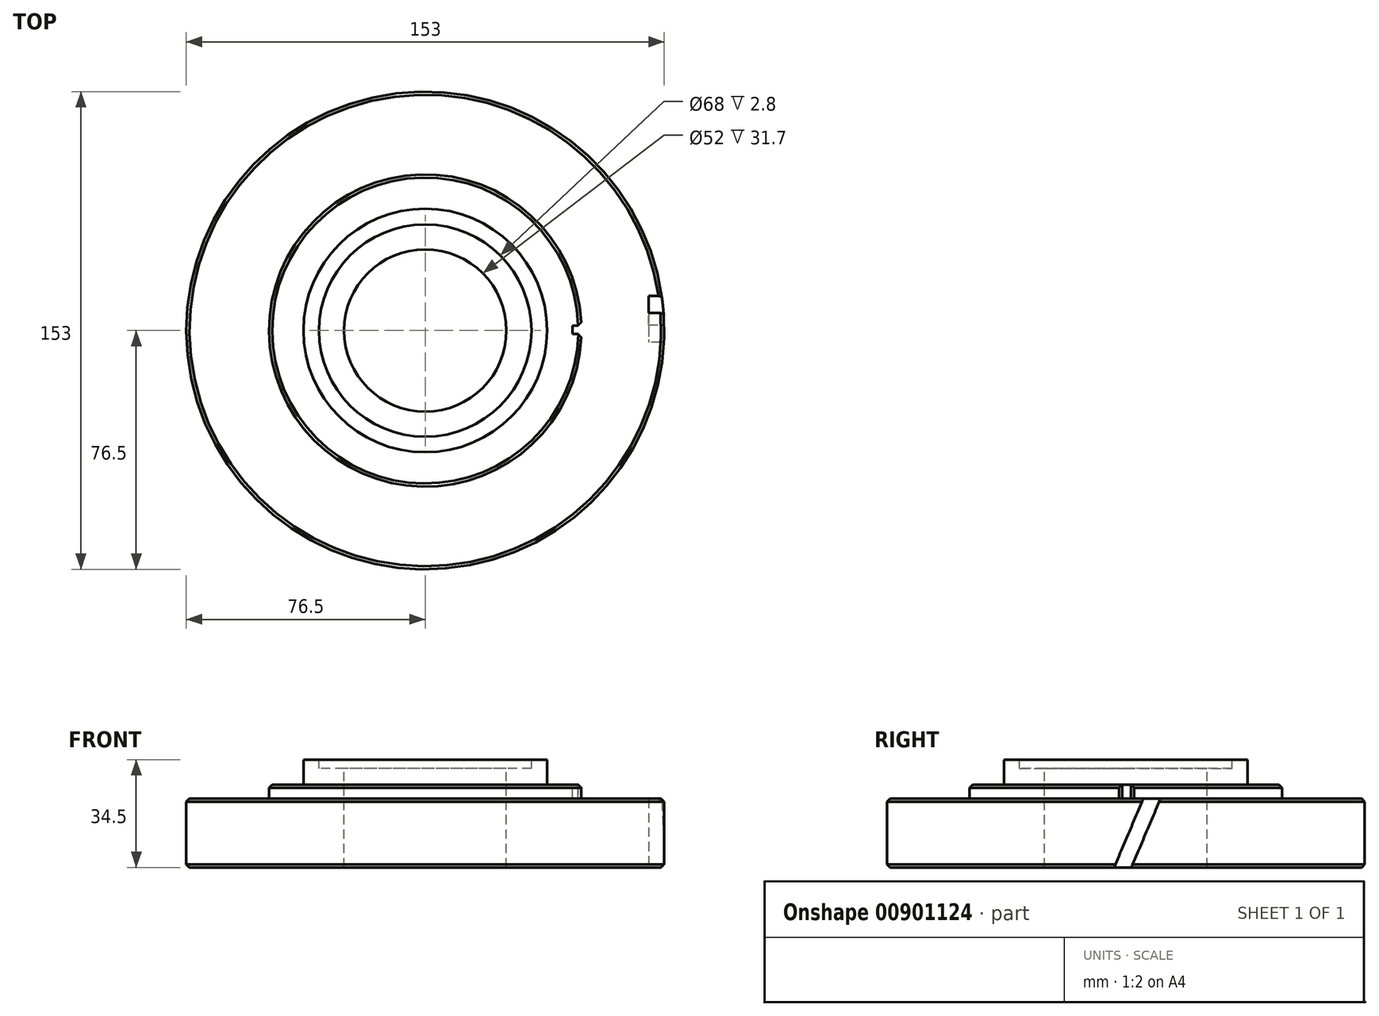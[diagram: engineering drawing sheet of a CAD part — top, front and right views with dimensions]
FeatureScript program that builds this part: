
annotation { "Feature Type Name" : "Feature", "Feature Type Description" : "" }
export const myFeature = defineFeature(function(context is Context, id is Id, definition is map)
    precondition{}
    {
        {
            var Q0;
            Q0=qCreatedBy(makeId("Front.planeOp"),FACE);
            var sketch = newSketch(context, id + "F0", { "sketchPlane" : qUnion([Q0])});
            skLineSegment(sketch, "E0", {"start": v(0, 34.5) * mm, "end": v(-39, 34.5) * mm});
            skLineSegment(sketch, "E1", {"start": v(-39, 34.5) * mm, "end": v(-39, 26.5) * mm});
            skLineSegment(sketch, "E2", {"start": v(-39, 26.5) * mm, "end": v(-50, 26.5) * mm});
            skLineSegment(sketch, "E3", {"start": v(-50, 26.5) * mm, "end": v(-50, 22) * mm});
            skLineSegment(sketch, "E4", {"start": v(-50, 22) * mm, "end": v(-76.5, 22) * mm});
            skLineSegment(sketch, "E5", {"start": v(-76.5, 22) * mm, "end": v(-76.5, 0) * mm});
            skLineSegment(sketch, "E6", {"start": v(-76.5, 0) * mm, "end": v(0, 0) * mm});
            skLineSegment(sketch, "E7", {"start": v(0, 0) * mm, "end": v(0, 34.5) * mm});
            skLineSegment(sketch, "E8", {"start": v(0, 59.57) * mm, "end": v(0, -27.66) * mm, "construction": true});
            skSolve(sketch);
        }
        {
            var Q0;
            Q0=makeQuery(id+"F0.imprint","IMPRINT",FACE,{"disambiguationData":[TD([[makeQuery(id+"F0.imprint","IMPRINT",EDGE,{"derivedFrom":sQuery(id+"F0.wireOp",EDGE,"E0")}),1.0]])]});
            var Q1;
            Q1=sQuery(id+"F0.wireOp",EDGE,"E8");
            revolve(context, id + "F1", {"surfaceOperationType" : NewSurfaceOperationType.NEW, "entities" : qUnion([Q0]), "axis" : qUnion([Q1]), "revolveType" : RevolveType.FULL});
        }
        {
            var Q0;
            Q0=makeQuery(id+"F1.opRevolve","SWEPT_FACE",FACE,{"disambiguationData":[OSD([sQuery(id+"F0.wireOp",EDGE,"E0")])]});
            var sketch = newSketch(context, id + "F2", { "sketchPlane" : qUnion([Q0])});
            skCircle(sketch, "E9", {"center": v(0, 0) * mm, "radius": 34 * mm});
            skSolve(sketch);
        }
        {
            var Q0;
            Q0 = qSketchRegion(id + "F2", true);
            extrude(context, id + "F3", {"entities" : qUnion([Q0]), "operationType" : NewBodyOperationType.REMOVE, "oppositeDirection" : true, "depth" : 2.8 * mm, "offsetDistance" : 25 * mm});
        }
        {
            var Q0;
            Q0=makeQuery(id+"F3.boolean.opBoolean","COPY",FACE,{"derivedFrom":makeQuery(id+"F3.opExtrude","CAP_FACE",FACE,{"disambiguationData":[OSD([sQuery(id+"F2.wireOp",EDGE,"E9")])],"isStart":false})});
            var sketch = newSketch(context, id + "F4", { "sketchPlane" : qUnion([Q0])});
            skCircle(sketch, "E10", {"center": v(0, 0) * mm, "radius": 26 * mm});
            skSolve(sketch);
        }
        {
            var Q0;
            Q0 = qSketchRegion(id + "F4", true);
            extrude(context, id + "F5", {"entities" : qUnion([Q0]), "operationType" : NewBodyOperationType.REMOVE, "endBound" : BoundingType.THROUGH_ALL, "oppositeDirection" : true, "depth" : 25 * mm, "offsetDistance" : 25 * mm});
        }
        {
            var Q0;
            Q0=qCreatedBy(makeId("Right.planeOp"),FACE);
            cPlane(context, id + "F6", {"entities" : qUnion([Q0]), "cplaneType" : CPlaneType.OFFSET, "offset" : 96.5 * mm, "width" : 150 * mm, "height" : 150 * mm});
        }
        {
            var Q0;
            Q0=qCreatedBy(id+"F6.planeOp",FACE);
            var sketch = newSketch(context, id + "F7", { "sketchPlane" : qUnion([Q0])});
            skLineSegment(sketch, "E11", {"start": v(12.66, 38.66) * mm, "end": v(-8.9, -12.16) * mm});
            skLineSegment(sketch, "E12", {"start": v(-8.9, -12.16) * mm, "end": v(-3.4, -12.16) * mm});
            skLineSegment(sketch, "E13", {"start": v(-3.4, -12.16) * mm, "end": v(18, 38.25) * mm});
            skLineSegment(sketch, "E14", {"start": v(18, 38.25) * mm, "end": v(12.66, 38.66) * mm});
            skSolve(sketch);
        }
        {
            var Q0;
            Q0=makeQuery(id+"F1.opRevolve","SWEPT_EDGE",EDGE,{"disambiguationData":[OSD([sQuery(id+"F0.wireOp",EDGE,"E4"),sQuery(id+"F0.wireOp",EDGE,"E5")])]});
            var Q1;
            Q1=makeQuery(id+"F1.opRevolve","SWEPT_EDGE",EDGE,{"disambiguationData":[OSD([sQuery(id+"F0.wireOp",EDGE,"E5"),sQuery(id+"F0.wireOp",EDGE,"E6")])]});
            var Q2;
            Q2=makeQuery(id+"F1.opRevolve","SWEPT_EDGE",EDGE,{"disambiguationData":[OSD([sQuery(id+"F0.wireOp",EDGE,"E2"),sQuery(id+"F0.wireOp",EDGE,"E3")])]});
            chamfer(context, id + "F8", {"entities" : qUnion([Q0, Q1, Q2]), "width" : 1 * mm, "tangentPropagation" : true});
        }
        {
            var Q0;
            Q0=makeQuery(id+"F7.imprint","IMPRINT",FACE,{"disambiguationData":[TD([[makeQuery(id+"F7.imprint","IMPRINT",EDGE,{"derivedFrom":sQuery(id+"F7.wireOp",EDGE,"E11")}),1.0]])]});
            extrude(context, id + "F9", {"entities" : qUnion([Q0]), "operationType" : NewBodyOperationType.REMOVE, "oppositeDirection" : true, "depth" : 25 * mm, "offsetDistance" : 25 * mm});
        }
        {
            var Q0;
            Q0=makeQuery(id+"F1.opRevolve","SWEPT_FACE",FACE,{"disambiguationData":[OSD([sQuery(id+"F0.wireOp",EDGE,"E2")])]});
            var sketch = newSketch(context, id + "F10", { "sketchPlane" : qUnion([Q0])});
            skLineSegment(sketch, "E15.bottom", {"start": v(47.18, -1.16) * mm, "end": v(53.25, -1.16) * mm});
            skLineSegment(sketch, "E15.top", {"start": v(47.18, 1.62) * mm, "end": v(53.25, 1.62) * mm});
            skLineSegment(sketch, "E15.left", {"start": v(47.18, -1.16) * mm, "end": v(47.18, 1.62) * mm});
            skLineSegment(sketch, "E15.right", {"start": v(53.25, -1.16) * mm, "end": v(53.25, 1.62) * mm});
            skSolve(sketch);
        }
        {
            var Q0;
            Q0 = qSketchRegion(id + "F10", true);
            var Q1;
            Q1=makeQuery(id+"F1.opRevolve","SWEPT_FACE",FACE,{"disambiguationData":[OSD([sQuery(id+"F0.wireOp",EDGE,"E4")])]});
            extrude(context, id + "F11", {"entities" : qUnion([Q0]), "operationType" : NewBodyOperationType.REMOVE, "endBound" : BoundingType.UP_TO_SURFACE, "oppositeDirection" : true, "depth" : 25 * mm, "endBoundEntityFace" : qUnion([Q1]), "offsetDistance" : 25 * mm});
        }
        {
            var Q0;
            Q0=makeQuery(id+"F11.boolean.opBoolean","INTERSECT",EDGE,{"derivedFrom":[makeQuery(id+"F1.opRevolve","SWEPT_FACE",FACE,{"disambiguationData":[OSD([sQuery(id+"F0.wireOp",EDGE,"E3")])]}),makeQuery(id+"F11.opExtrude","SWEPT_FACE",FACE,{"disambiguationData":[OSD([sQuery(id+"F10.wireOp",EDGE,"E15.bottom")])]})]});
            var Q1;
            Q1=makeQuery(id+"F11.boolean.opBoolean","INTERSECT",EDGE,{"derivedFrom":[makeQuery(id+"F1.opRevolve","SWEPT_FACE",FACE,{"disambiguationData":[OSD([sQuery(id+"F0.wireOp",EDGE,"E3")])]}),makeQuery(id+"F11.opExtrude","SWEPT_FACE",FACE,{"disambiguationData":[OSD([sQuery(id+"F10.wireOp",EDGE,"E15.top")])]})]});
            chamfer(context, id + "F12", {"entities" : qUnion([Q0, Q1]), "width" : 1 * mm, "tangentPropagation" : true});
        }
    });
